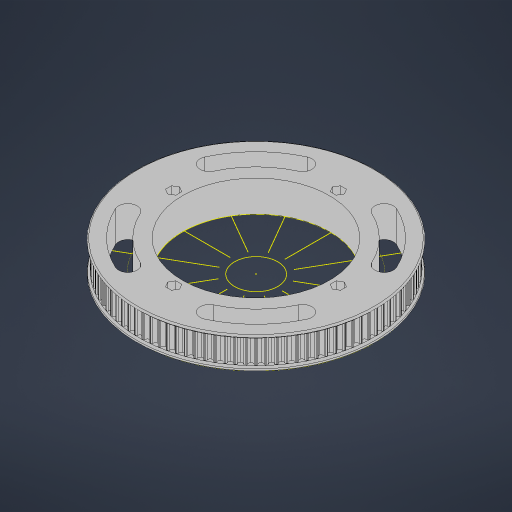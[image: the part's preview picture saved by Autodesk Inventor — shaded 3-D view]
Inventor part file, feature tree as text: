
AUTODESK INVENTOR PART (.ipt)
format: ipt  version: 2024 (Build 280153000, 153)  size: 1,500,672 bytes
history: native  units: mm
features: extrude x8, sketch x6, other x4, fillet x3, pattern_circular x2, revolve x1, mirror x1, hole x1, reference x1, projected_geometry x1
ambient origin geometry x8: Origin, YZ Plane, XZ Plane, XY Plane, X Axis, Y Axis, Z Axis, Center Point
bodies: Solid1 (feature_tree)
feature tree (28):
  extrude  "Extrusion1"  Depth=21.0mm
  extrude  "Extrusion2"  Depth=5.8mm
  extrude  "Extrusion3"  Depth=21.0mm
  fillet  "Fillet2"  [1 undecoded]
  pattern_circular  "Circular Pattern1"  [2 undecoded]
  revolve  "Revolution2"  [1 undecoded]
  mirror  "Mirror2"
  fillet  "Fillet5"  [1 undecoded]
  extrude  "Extrusion4"  TaperAngle=90.0deg  [1 undecoded]
  pattern_circular  "Circular Pattern2"  [2 undecoded]
  sketch  "Sketch7"  dims[d10=0.6mm]
  extrude  "Extrusion5"  Depth=2.5mm
  extrude  "Extrusion6"  Depth=19.5mm
  hole  "Hole1"  [1 undecoded]
  extrude  "Extrusion7"  Depth=2.5mm
  extrude  "Extrusion9"  Depth=2.5mm
  fillet  "Fillet1"  Radius=0.8mm
  sketch  "Sketch2"  dims[d0=29.0mm d2=21.0mm]
  sketch  "Sketch5"  dims[d3=0.0mm d5=5.8mm]
  sketch  "Sketch6"  dims[d7=1.565mm d8=21.0mm d9=0.0mm]
  reference  "Reference1"
  projected_geometry  "Projected Loop1"
  sketch  "Sketch8"  dims[d12=159.154943mm]
  sketch  "Sketch10"  dims[d13=0.0mm d14=0.0mm d15=0.6mm d16=1000.0mm d17=360.0deg d35=90.0deg d36=0.0mm d37=2.5mm d38=76.577472mm d39=5.1mm d40=2.5mm d41=2.5mm d42=0.8mm d43=0.05mm d44=75.577472mm d45=18.5mm d46=10.0mm d47=0.0mm d48=120.0mm d49=360.0deg d51=10.0mm d52=0.0mm d53=10.0mm d54=0.0mm d55=5.3mm d56=6.0mm d57=10.4mm d58=2.0mm d59=90.0deg d60=8.0mm d61=20.594885mm d62=7.0mm d63=40.0mm d65=360.0deg d67=19.5mm d68=0.0mm d73=65.0mm d74=65.0mm d75=3.490659mm d76=65.0mm d77=6.981317mm d78=12.5mm d79=135.0deg d80=40.0mm d82=360.0deg d84=0.0mm d85=0.0mm d71=0.0mm d72=0.0mm]
  other  "<userpath>\CodingProjects\C-AAM\CAD\V1\Base.iam"
  other  "Base.iam"
  other  "LazySusan:1"
  other  "IR:1"
note: 9 required parameter values undecoded (feature->parameter linkage not recoverable at this tier; creation-order binding heuristic only, values carry confidence <= 0.55)